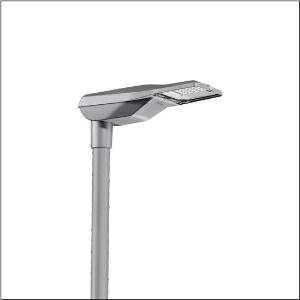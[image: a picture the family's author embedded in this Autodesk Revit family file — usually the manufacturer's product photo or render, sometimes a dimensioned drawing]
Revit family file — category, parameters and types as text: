
# Revit family: streetlight_sl_21_iq_micro___st0_8a_5xe1c21d08cb_82e6
name_source: partatom
category: Lighting Fixtures
units: mm (PartAtom-declared; Revit-internal decimal feet)

## family parameters
Cut with Voids When Loaded = No
Host = Face
Light Source = No
Part Type = Normal
Room Calculation Point = No
Round Connector Dimension = Use Diameter
Shared = No

## types (1)
- --- (1 x LED, 2380 lm, 19.4 W, 2200K)
    Apparent Load = 19 VA
    CIE Flux Codes = 38 75 97 100 100
    Color Rendering = 70
    Color Temperature = 2200K
    Default Elevation = 1800 mm
    Description = Streetlight SL 21 iQ micro, mast luminaire, primary light control with lens, of PMMA, primary optical cover: cover, of toughened safety glass, transparent, light distribution: ST0.8a, light emission: direct distribution, primary light characteristic: asymmetric, installation type: post-top, side-entry, LED, High Power LED, rated luminous flux: 2.380lm, luminous efficacy: 123lm/W, light colour: 722, colour temperature: 2200K, control: Auto-Match, Temp-Guard, Lumen-Switch, Night-Set, Smart-Wire, Light-Fading, Desk-Remote (wireless, voltage-free reading and setting of iQ features in the workshop via application-optimized NFC function/RFID function), optimised constant luminous flux control (CLO 2.0), presetting dimming linear, mains connection: 220..240V, AC, 50/60Hz, start of lifetime: 19W, end of service life: 20W, reduction: 10W, luminaire housing, of diecast aluminium, powder-coated, Siteco® metallic grey (DB 702S), corrosivity category C5 mid according to DIN EN ISO 12944, please order mast flange separately, inclination adjustable: 0°, 5°, 10°, 15°, sealing non-destructively replaceable, multi-level sealing system, length: 528mm, width: 235mm, height: 110mm, mast flange for spigot size: 42mm (side-entry): 5XC10008XM4, 60/48mm (side-entry/post-top): 5XC10108XM2, 76/60mm (side-entry/post-top): 5XC10108XM1, protection rating (complete): IP66, insulation class (complete): insulation class II (safety insulation), certification: CE, ENEC, ENEC+, VDE, impact resistance: IK09, permissible operating ambient temperature for outdoor applications: -40..+50°C, standard-compliant lighting for roads and squares, packaging unit: 1 piece

Light Distribution: ST0.8a
    Height = 110 mm
    Lamp = 1 x LED
    Lamp Light Flux = 2380 lm
    Lamp Power = 19.4 W
    Lamp count = 1
    Length = 528 mm
    Luminous efficacy = 123 lm/W
    Manufacturer = Siteco
    ModVariant = No
    Model = 5XE1C21D08CB
    Number of Poles = 1
    OnlyDefault = Yes
    Power Factor = 1
    Product Name = Streetlight SL 21 iQ micro | ST0.8a
    Product group = mast luminaire | pylon top
    ProductGroupID = 6100
    Protection Class = Protection class II
    Protection Degree = IP 66
    RLX_Detail_Level = 1
    RLX_Emergency_Light_Flux = 0 lm
    RLX_Emergency_Type = 0
    RLX_Emergency_Type_DB = No
    RlxData = <blob elided: 98649 chars, md5=eb658574>
    Socket = socket
    Standby Power = 0 W
    System Light Flux = 2380 lm
    System Power = 19 W
    Type Comments = factory setting: luminous flux: 100 % | dim-lin: 254 | 387 mA
    Type Image = l_1006881.jpg
    URL = http://relux.com
    VarID = @adj_087905
    Voltage = 0 V
    Weight = 0.00 kg
    Width = 235 mm

## geometry (parser evidence)
native form markers: Blend x4, Sweep x10
no freeform markers — native parametric forms only
